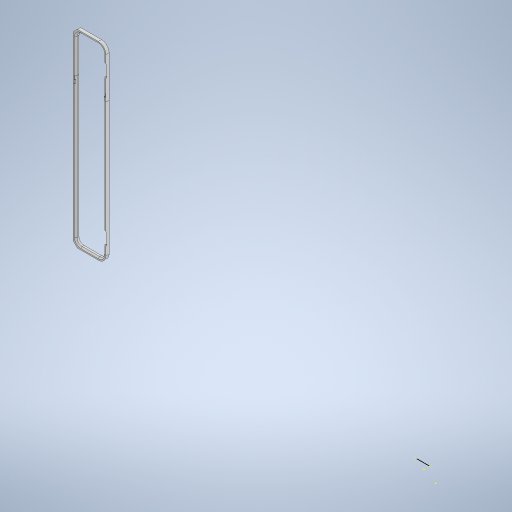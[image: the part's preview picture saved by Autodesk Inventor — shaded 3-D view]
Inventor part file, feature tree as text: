
AUTODESK INVENTOR PART (.ipt)
format: ipt  version: 2024.1 (Build 281209000, 209)  size: 7,057,408 bytes
history: native  units: mm
features: projected_geometry x112, sketch x92, extrude x87, chamfer x77, other x33, plane x15, fillet x9, pattern_linear x7, mirror x3, loft x2, pattern_circular x1, sweep x1
ambient origin geometry x8: Origin, YZ Plane, XZ Plane, XY Plane, X Axis, Y Axis, Z Axis, Center Point
bodies: Solid3 (feature_tree), Solid4 (feature_tree), Solid8 (feature_tree), Solid9 (feature_tree), Solid14 (feature_tree), Solid16 (feature_tree), Solid26 (feature_tree), Solid27 (feature_tree)
feature tree (439):
  other  "synth-a"
  other  "Blocks"
  extrude  "Extrusion1"  Depth=30.22mm
  plane  "Work Plane1"
  extrude  "Extrusion2"  Depth=17.13mm
  plane  "Work Plane2"
  mirror  "Mirror1"
  sketch  "Sketch3"  dims[d5=2.61mm d6=226.0mm]
  extrude  "Extrusion3"  Depth=226.0mm
  extrude  "Extrusion4"  Depth=8.2mm
  extrude  "Extrusion5"  Depth=35.4mm
  fillet  "Fillet1"  Radius=7.89mm
  pattern_linear  "Rectangular Pattern1"  Count1=56 Spacing1=0.0mm
  extrude  "Extrusion6"  Depth=3.14mm
  chamfer  "Chamfer1"  Distance=13.85mm
  chamfer  "Chamfer2"  Distance=440.5mm
  chamfer  "Chamfer3"  Distance=11.2mm
  chamfer  "Chamfer4"  Distance=3.1mm
  chamfer  "Chamfer5"  Distance=20.0mm
  chamfer  "Chamfer6"  Distance=7.26mm
  chamfer  "Chamfer7"  Distance=7.0mm Angle=45.0deg
  chamfer  "Chamfer8"  Distance=7.0mm Angle=45.0deg
  chamfer  "Chamfer9"  Distance=7.0mm Angle=45.0deg
  chamfer  "Chamfer10"  Distance=7.0mm Angle=45.0deg
  chamfer  "Chamfer11"  Distance=7.0mm Angle=45.0deg
  chamfer  "Chamfer12"  Distance=7.0mm Angle=45.0deg
  chamfer  "Chamfer13"  Distance=7.0mm Angle=45.0deg
  chamfer  "Chamfer14"  Distance=7.0mm Angle=45.0deg
  chamfer  "Chamfer15"  Distance=7.0mm Angle=45.0deg
  fillet  "Fillet2"  Radius=1.5mm
  pattern_linear  "Rectangular Pattern2"  Count1=3  [1 undecoded]
  extrude  "Extrusion7"  Depth=40.0mm
  extrude  "Extrusion8"  Depth=40.0mm
  plane  "Work Plane3"
  extrude  "Extrusion9"  Depth=20.42mm TaperAngle=0.0deg
  plane  "Work Plane7"
  plane  "Work Plane9"
  extrude  "Extrusion18"  Depth=60.6mm
  sketch  "Sketch26"  dims[d46=3.63mm]
  extrude  "Extrusion24"  Depth=35.8mm
  extrude  "Extrusion25"  Depth=2.9mm TaperAngle=0.0deg
  fillet  "Fillet3"  [1 undecoded]
  extrude  "Extrusion10"  Depth=20.0mm
  sketch  "Sketch12"  dims[d25=18.04mm]
  plane  "Work Plane5"
  extrude  "Extrusion12"  Depth=20.0mm
  extrude  "Extrusion14"  Depth=20.0mm
  extrude  "Extrusion15"  Depth=5.0mm
  plane  "Work Plane6"
  extrude  "Extrusion16"  Depth=16.580628mm
  mirror  "Mirror2"
  extrude  "Extrusion77"  Depth=20.0mm
  extrude  "Extrusion78"  Depth=5.0mm
  extrude  "Extrusion79"  Depth=2.0mm
  extrude  "Extrusion80"  Depth=2.5mm
  extrude  "Extrusion81"  Depth=2.5mm
  extrude  "Extrusion82"  Depth=2.5mm
  pattern_linear  "Rectangular Pattern4"  Count1=3 Spacing1=241.0mm
  chamfer  "Chamfer64"  Distance=10.0mm
  chamfer  "Chamfer65"  Distance=0.01mm
  chamfer  "Chamfer66"  Distance=10.0mm
  pattern_linear  "Rectangular Pattern3"  Count1=2 Spacing1=105.0mm
  pattern_linear  "Rectangular Pattern10"  Count1=2 Spacing1=0.0mm
  extrude  "Extrusion17"  Depth=2.0mm
  extrude  "Extrusion56"  Depth=4.0mm
  extrude  "Extrusion57"  Depth=3.0mm
  plane  "Work Plane8"
  plane  "Work Plane11"
  extrude  "Extrusion33"  Depth=4.0mm
  fillet  "Fillet6"  Radius=1.0mm
  extrude  "Extrusion29"  Depth=2.0mm
  extrude  "Extrusion31"  Depth=10.0mm
  extrude  "Extrusion32"  Depth=292.1mm
  extrude  "Extrusion34"  Depth=8.0mm
  extrude  "Extrusion35"  Depth=0.5mm TaperAngle=0.0deg
  extrude  "Extrusion36"  Depth=28.3mm
  fillet  "Fillet7"  Radius=28.3mm
  pattern_circular  "Circular Pattern1"  Count=7  [1 undecoded]
  extrude  "Extrusion37"  Depth=11.3mm
  plane  "Work Plane17"
  extrude  "Extrusion38"  Depth=13.54mm
  extrude  "Extrusion39"  Depth=22.0mm
  extrude  "Extrusion40"  Depth=2.0mm
  extrude  "Extrusion41"  Depth=2.0mm
  extrude  "Extrusion43"  Depth=2.0mm
  extrude  "Extrusion44"  Depth=2.0mm TaperAngle=0.0deg
  sketch  "Sketch47"  dims[d121=20.0mm d122=0.0mm d123=5.0mm]
  chamfer  "Chamfer18"  Distance=2.0mm Angle=45.0deg
  chamfer  "Chamfer19"  Distance=2.0mm
  chamfer  "Chamfer20"  Distance=13.0mm
  extrude  "Extrusion45"  Depth=2.0mm
  chamfer  "Chamfer21"  Distance=26.0mm
  extrude  "Extrusion46"  Depth=2.0mm TaperAngle=0.0deg
  extrude  "Extrusion49"  Depth=11.0mm
  extrude  "Extrusion50"  Depth=2.0mm TaperAngle=0.0deg
  plane  "Work Plane13"
  extrude  "Extrusion51"  Depth=10.0mm TaperAngle=0.0deg
  pattern_linear  "Rectangular Pattern7"  Spacing1=4.0mm  [1 undecoded]
  extrude  "Extrusion52"  Depth=2.0mm TaperAngle=0.0deg
  extrude  "Extrusion53"  Depth=2.0mm
  extrude  "Extrusion54"  Depth=2.0mm TaperAngle=0.0deg
  extrude  "Extrusion55"  Depth=2.0mm TaperAngle=45.0deg
  chamfer  "Chamfer22"  Distance=2.0mm
  chamfer  "Chamfer23"  Distance=150.0mm
  chamfer  "Chamfer24"  Distance=0.02mm
  chamfer  "Chamfer25"  Distance=15.0mm
  extrude  "Extrusion74"  Depth=2.0mm TaperAngle=0.0deg
  chamfer  "Chamfer58"  Distance=7.0mm
  chamfer  "Chamfer59"  Distance=5.0mm
  plane  "Work Plane16"
  extrude  "Extrusion73"  Depth=2.0mm
  plane  "Work Plane14"
  extrude  "Extrusion75"  Depth=2.0mm
  chamfer  "Chamfer60"  Distance=2.5mm
  plane  "Work Plane15"
  extrude  "Extrusion71"  Depth=2.0mm TaperAngle=0.0deg
  extrude  "Extrusion72"  Depth=2.0mm
  chamfer  "Chamfer61"  Distance=7.0mm
  chamfer  "Chamfer62"  Distance=10.5mm
  extrude  "Extrusion83"  Depth=241.0mm
  extrude  "Extrusion84"  Depth=2.0mm
  extrude  "Extrusion85"  Depth=2.0mm
  extrude  "Extrusion86"  TaperAngle=90.0deg  [1 undecoded]
  extrude  "Extrusion87"  Depth=2.0mm
  loft  "Loft2"
  chamfer  "Chamfer68"  Distance=420.0mm
  chamfer  "Chamfer69"  Distance=7.0mm
  chamfer  "Chamfer70"  Distance=40.0mm
  chamfer  "Chamfer71"  Distance=7.0mm
  chamfer  "Chamfer72"  Distance=10.0mm
  chamfer  "Chamfer73"  Distance=4.2mm
  chamfer  "Chamfer79"  [1 undecoded]
  chamfer  "Chamfer80"  Distance=2.5mm
  chamfer  "Chamfer81"  Distance=8.0mm
  chamfer  "Chamfer82"  Distance=10.0mm
  chamfer  "Chamfer83"  Distance=1.5mm
  sketch  "Sketch109"  dims[d216=16.2mm d217=28.3mm d218=28.3mm]
  extrude  "Extrusion91"  Depth=1.0mm
  chamfer  "Chamfer84"  Distance=1.0mm
  chamfer  "Chamfer85"  Distance=160.0mm Angle=360.0deg
  chamfer  "Chamfer86"  Distance=13.0mm
  chamfer  "Chamfer87"  Distance=1.5mm
  pattern_linear  "Rectangular Pattern9"  Spacing1=1.2mm  [1 undecoded]
  extrude  "Extrusion58"  Depth=2.0mm TaperAngle=0.0deg
  extrude  "Extrusion59"  Depth=2.0mm TaperAngle=0.0deg
  chamfer  "Chamfer26"  Distance=7.1mm
  chamfer  "Chamfer27"  Distance=2.0mm
  chamfer  "Chamfer28"  Distance=8.8mm
  chamfer  "Chamfer29"  Distance=48.0mm
  chamfer  "Chamfer30"  Distance=30.0mm
  chamfer  "Chamfer31"  Distance=40.0mm
  chamfer  "Chamfer32"  Distance=43.0mm
  extrude  "Extrusion60"  Depth=2.0mm
  extrude  "Extrusion61"  Depth=2.0mm
  loft  "Loft1"
  extrude  "Extrusion62"  Depth=2.0mm
  sweep  "Sweep1"
  chamfer  "Chamfer33"  Distance=11.5mm
  chamfer  "Chamfer35"  Distance=8.0mm
  chamfer  "Chamfer36"  Distance=4.0mm
  extrude  "audio-io-device"  Depth=2.0mm
  fillet  "Fillet4"  Radius=3.0mm
  extrude  "Extrusion20"  Depth=10.0mm TaperAngle=0.0deg
  extrude  "Extrusion21"  Depth=10.0mm TaperAngle=0.0deg
  extrude  "Extrusion22"  Depth=8.0mm TaperAngle=45.0deg
  chamfer  "Chamfer16"  Distance=2.0mm Angle=45.0deg
  fillet  "Fillet5"  Radius=4.0mm
  extrude  "Extrusion23"  Depth=2.0mm
  extrude  "Extrusion92"  Depth=23.0mm
  fillet  "Fillet8"  Radius=10.0mm
  extrude  "Extrusion26"  Depth=20.0mm
  extrude  "Extrusion27"  Depth=8.0mm TaperAngle=45.0deg
  chamfer  "Chamfer17"  Distance=2.5mm
  plane  "Work Plane10"
  mirror  "Mirror3"
  extrude  "Extrusion28"  Depth=10.0mm
  extrude  "io-device-clip"  Depth=10.0mm TaperAngle=0.0deg
  extrude  "Extrusion93"  Depth=20.0mm
  fillet  "Fillet9"  Radius=1.5mm
  extrude  "Extrusion64"  Depth=2.0mm
  extrude  "Extrusion65"  Depth=1.0mm
  extrude  "Extrusion66"  Depth=1.0mm
  extrude  "Extrusion67"  Depth=5.75mm
  chamfer  "Chamfer38"  Distance=3.0mm
  extrude  "Extrusion69"  Depth=2.0mm
  extrude  "Extrusion70"  Depth=2.0mm
  chamfer  "Chamfer48"  Angle=90.0deg  [1 undecoded]
  chamfer  "Chamfer49"  Distance=1.5mm
  chamfer  "Chamfer50"  Distance=1.5mm
  chamfer  "Chamfer51"  Distance=1.5mm
  chamfer  "Chamfer52"  Distance=1.5mm
  chamfer  "Chamfer53"  Distance=1.5mm
  chamfer  "Chamfer54"  Distance=1.5mm
  chamfer  "Chamfer55"  Distance=9.0mm
  chamfer  "Chamfer56"  Distance=4.0mm
  chamfer  "Chamfer57"  Distance=9.0mm
  chamfer  "Chamfer74"  Distance=10.0mm
  chamfer  "Chamfer75"  Distance=20.0mm
  chamfer  "Chamfer76"  Distance=0.02mm
  chamfer  "Chamfer77"  Distance=0.02mm
  chamfer  "Chamfer78"  Distance=9.0mm
  extrude  "Extrusion88"  Depth=15.0mm TaperAngle=0.0deg
  extrude  "Extrusion89"  Depth=22.0mm
  extrude  "Extrusion94"  Depth=2.0mm
  extrude  "Extrusion95"  Depth=2.0mm TaperAngle=0.0deg
  chamfer  "Chamfer88"  Distance=4.5mm
  chamfer  "Chamfer89"  Distance=48.0mm
  chamfer  "Chamfer90"  Distance=9.0mm
  extrude  "Extrusion96"  Depth=2.0mm
  sketch  "Sketch1"  dims[d0=205.0mm d1=30.22mm]
  sketch  "Sketch2"  dims[d2=102.5mm d3=17.13mm]
  projected_geometry  "Projected Loop1"
  sketch  "Sketch4"  dims[d7=12.4mm d8=8.2mm]
  projected_geometry  "Projected Loop2"
  sketch  "Sketch5"  dims[d9=4.5mm d10=35.4mm d11=7.89mm]
  sketch  "Sketch6"  dims[d12=9.657689mm]
  projected_geometry  "Projected Loop3"
  sketch  "Sketch7"  dims[d13=17.466067mm d14=560.0mm d15=0.0mm]
  sketch  "Sketch8"  dims[d16=-18.52mm d17=3.14mm d18=13.85mm d19=0.0mm]
  sketch  "Sketch9"  dims[d20=17.38mm]
  sketch  "Sketch10"  dims[d21=91.58mm d22=440.5mm d23=0.0mm]
  projected_geometry  "Projected Loop4"
  projected_geometry  "Projected Loop5"
  projected_geometry  "Projected Loop6"
  other  "stand-leg-A"
  other  "Pattern of stand-leg-A:1"
  other  "Pattern of stand-leg-A:2"
  sketch  "Sketch11"  dims[d24=2.4mm]
  sketch  "Sketch14"  dims[d26=18.56mm d27=11.2mm d28=0.0mm]
  projected_geometry  "Projected Loop8"
  sketch  "Sketch15"  dims[d29=81.62mm d30=3.1mm d31=0.0mm]
  sketch  "Sketch17"  dims[d32=1.5mm d33=220.0mm d35=20.0mm]
  projected_geometry  "Projected Loop10"
  projected_geometry  "Projected Loop11"
  projected_geometry  "Projected Loop12"
  projected_geometry  "Projected Loop13"
  sketch  "Sketch18"  dims[d36=48.6mm]
  sketch  "Sketch19"  dims[d37=8.7mm]
  projected_geometry  "Projected Loop14"
  projected_geometry  "Projected Loop15"
  projected_geometry  "Projected Loop16"
  projected_geometry  "Projected Loop17"
  projected_geometry  "Projected Loop18"
  projected_geometry  "Projected Loop19"
  projected_geometry  "Projected Loop20"
  projected_geometry  "Projected Loop21"
  other  "crossbars"
  sketch  "Sketch20"  dims[d38=8.7mm]
  sketch  "Sketch21"  dims[d39=8.7mm]
  other  "audio-io"
  sketch  "Sketch22"  dims[d40=8.7mm]
  projected_geometry  "Projected Loop22"
  sketch  "Sketch23"  dims[d41=8.7mm]
  sketch  "Sketch24"  dims[d44=3.63mm]
  sketch  "Sketch25"  dims[d45=3.63mm]
  projected_geometry  "Projected Loop23"
  sketch  "Sketch27"  dims[d47=3.63mm]
  projected_geometry  "Projected Loop24"
  other  "audio-io-stand"
  sketch  "Sketch28"  dims[d48=3.63mm]
  projected_geometry  "Projected Loop25"
  sketch  "Sketch29"  dims[d49=3.63mm d50=7.26mm d51=0.0mm d52=5.0mm d53=7.0mm d54=45.0deg d55=5.0mm d56=7.0mm d57=45.0deg d58=5.0mm d59=7.0mm d60=45.0deg d61=5.0mm d62=7.0mm d63=45.0deg d64=5.0mm d65=7.0mm d66=45.0deg d67=1.5mm d68=7.0mm d69=45.0deg d70=1.5mm d71=7.0mm d72=45.0deg d73=1.5mm d74=7.0mm d75=45.0deg d76=1.5mm d77=7.0mm d78=45.0deg]
  sketch  "Sketch30"  dims[d79=1.5mm d80=7.0mm d81=45.0deg]
  projected_geometry  "Projected Loop26"
  sketch  "Sketch34"  dims[d82=1.5mm d83=7.0mm d84=45.0deg]
  projected_geometry  "Projected Loop29"
  sketch  "Sketch35"  dims[d85=1.5mm d86=7.0mm d87=45.0deg]
  other  "back-uprights"
  projected_geometry  "Projected Loop30"
  sketch  "Sketch36"  dims[d88=1.5mm d89=7.0mm d90=45.0deg]
  other  "looper"
  sketch  "Sketch37"  dims[d91=1.5mm d92=7.0mm d93=45.0deg]
  sketch  "Sketch38"  dims[d94=1.5mm d95=7.0mm d96=45.0deg d97=1.5mm d98=30.0mm d100=140.0mm]
  sketch  "Sketch39"  dims[d101=17.93mm d102=40.0mm]
  sketch  "Sketch40"  dims[d103=40.0mm d104=40.0mm]
  sketch  "Sketch41"  dims[d105=35.4mm d106=20.42mm d107=0.0mm]
  projected_geometry  "Projected Loop31"
  projected_geometry  "Projected Loop32"
  other  "top-arm"
  sketch  "Sketch42"  dims[d108=20.16mm d109=60.6mm]
  projected_geometry  "Projected Loop33"
  sketch  "Sketch43"  dims[d110=60.6mm d111=35.8mm]
  projected_geometry  "Projected Loop34"
  sketch  "Sketch44"  dims[d112=52.9mm d113=2.9mm d114=0.0mm d115=-10.0mm]
  sketch  "Sketch45"  dims[d116=20.0mm d118=90.0mm]
  projected_geometry  "Projected Loop35"
  sketch  "Sketch46"  dims[d119=10.0mm d120=20.0mm]
  projected_geometry  "Projected Loop36"
  projected_geometry  "Projected Loop37"
  sketch  "Sketch48"  dims[d124=5.0mm d125=5.0mm]
  projected_geometry  "Projected Loop38"
  sketch  "Sketch50"  dims[d126=30.0mm d127=16.580628mm]
  projected_geometry  "Projected Loop40"
  other  "Pattern of back-uprights:3"
  other  "Pattern of back-uprights:4"
  sketch  "Sketch57"  dims[d128=8.0mm d129=20.0mm]
  projected_geometry  "Projected Loop42"
  projected_geometry  "Projected Loop43"
  sketch  "Sketch58"  dims[d133=5.0mm d134=5.0mm]
  projected_geometry  "Projected Loop44"
  sketch  "Sketch59"  dims[d135=18.0mm d136=2.0mm]
  projected_geometry  "Projected Loop45"
  projected_geometry  "Projected Loop46"
  projected_geometry  "Projected Loop47"
  sketch  "Sketch60"  dims[d139=120.0mm d140=2.5mm]
  projected_geometry  "Projected Loop48"
  projected_geometry  "Projected Loop49"
  other  "back-crossbeam"
  sketch  "Sketch61"  dims[d141=2.5mm d142=2.5mm]
  projected_geometry  "Projected Loop50"
  sketch  "Sketch62"  dims[d143=2.5mm d144=2.5mm]
  other  "sqr-connector"
  other  "sqr-connector_1"
  other  "sqr-connector_2"
  sketch  "Sketch63"  dims[d145=2.5mm]
  projected_geometry  "Projected Loop51"
  projected_geometry  "Projected Loop52"
  projected_geometry  "Projected Loop53"
  sketch  "Sketch66"  dims[d146=95.0mm]
  projected_geometry  "Projected Loop55"
  sketch  "Sketch67"  dims[d147=2.5mm d148=30.0mm d150=241.0mm]
  projected_geometry  "Projected Loop56"
  projected_geometry  "Projected Loop57"
  projected_geometry  "Projected Loop58"
  projected_geometry  "Projected Loop59"
  projected_geometry  "Projected Loop60"
  projected_geometry  "Projected Loop61"
  projected_geometry  "Projected Loop62"
  projected_geometry  "Projected Loop63"
  projected_geometry  "Projected Loop64"
  projected_geometry  "Projected Loop65"
  sketch  "Sketch68"  dims[d151=2.0mm]
  projected_geometry  "Projected Loop66"
  projected_geometry  "Projected Loop67"
  sketch  "Sketch69"  dims[d152=10.0mm]
  projected_geometry  "Projected Loop68"
  projected_geometry  "Projected Loop69"
  other  "TOP-CROSSBEAM"
  sketch  "Sketch70"  dims[d153=7.0mm]
  projected_geometry  "Projected Loop70"
  other  "angled-member"
  sketch  "Sketch71"  dims[d154=10.0mm]
  projected_geometry  "Projected Loop71"
  other  "Edges1"
  other  "Edges2"
  sketch  "Sketch74"  dims[d155=6.5mm]
  projected_geometry  "Projected Loop74"
  sketch  "Sketch75"  dims[d156=6.5mm]
  projected_geometry  "Projected Loop75"
  sketch  "Sketch76"  dims[d158=0.01mm]
  sketch  "Sketch77"  dims[d159=5.0mm]
  projected_geometry  "Projected Loop76"
  sketch  "Sketch78"  dims[d161=8.0mm]
  projected_geometry  "Projected Loop77"
  sketch  "Sketch79"  dims[d162=0.01mm]
  projected_geometry  "Projected Loop78"
  sketch  "Sketch80"  dims[d163=15.0mm]
  projected_geometry  "Projected Loop79"
  projected_geometry  "Projected Loop80"
  projected_geometry  "Projected Loop81"
  sketch  "Sketch81"  dims[d164=2.0mm d165=10.0mm d166=0.0mm d169=0.01mm d170=0.0mm]
  projected_geometry  "Projected Loop82"
  sketch  "Sketch83"  dims[d171=0.01mm d174=10.0mm d175=0.0mm]
  sketch  "Sketch85"  dims[d176=0.01mm d177=0.0mm]
  projected_geometry  "Projected Loop83"
  projected_geometry  "Projected Loop84"
  projected_geometry  "Projected Loop85"
  sketch  "Sketch86"  dims[d178=8.0mm]
  sketch  "Sketch88"  dims[d179=7.0mm]
  sketch  "Sketch89"  dims[d180=-8.0mm]
  projected_geometry  "Projected Loop87"
  sketch  "Sketch90"  dims[d181=6.0mm]
  projected_geometry  "Projected Loop88"
  sketch  "Sketch91"  dims[d182=4.0mm]
  sketch  "Sketch94"  dims[d183=3.0mm]
  sketch  "Sketch95"  dims[d184=3.0mm]
  sketch  "Sketch96"  dims[d185=2.0mm]
  projected_geometry  "Projected Loop90"
  projected_geometry  "Projected Loop91"
  sketch  "Sketch97"  dims[d186=7.0mm d187=0.0mm d188=20.0mm d190=105.0mm d191=20.0mm d192=0.0mm]
  projected_geometry  "Projected Loop92"
  projected_geometry  "Projected Loop93"
  projected_geometry  "Projected Loop94"
  projected_geometry  "Projected Loop95"
  other  "feet"
  sketch  "Sketch98"  dims[d193=2.5mm d194=2.0mm]
  projected_geometry  "Projected Loop96"
  projected_geometry  "Projected Loop97"
  other  "rubber-top-base"
  sketch  "Sketch99"  dims[d195=90.0deg d196=4.0mm d197=7.0mm]
  projected_geometry  "Projected Loop98"
  other  "rubber-stopper"
  other  "Pattern of feet:7"
  other  "Pattern of feet:8"
  sketch  "Sketch100"  dims[d198=4.5mm d199=3.0mm]
  projected_geometry  "Projected Loop99"
  projected_geometry  "Projected Loop100"
  projected_geometry  "Projected Loop101"
  projected_geometry  "Projected Loop102"
  other  "rubber-toppers-top"
  sketch  "Sketch101"  dims[d200=4.0mm d201=4.0mm d202=1.0mm]
  projected_geometry  "Projected Loop103"
  other  "rubber-cap"
  sketch  "Sketch102"  dims[d203=7.0mm d204=2.0mm]
  projected_geometry  "Projected Loop104"
  other  "rubber-tip"
  sketch  "Sketch103"  dims[d205=13.0mm d206=0.0mm d207=10.0mm]
  projected_geometry  "Projected Loop105"
  sketch  "Sketch104"  dims[d208=107.0mm d209=292.1mm]
  projected_geometry  "Projected Loop106"
  other  "Edges3"
  other  "Edges4"
  sketch  "Sketch105"  dims[d210=43.8mm d211=0.0mm d212=8.0mm]
  projected_geometry  "Projected Loop107"
  sketch  "Sketch106"  dims[d213=1.59mm d214=0.5mm d215=0.0mm]
  projected_geometry  "Projected Loop108"
  projected_geometry  "Projected Loop110"
  sketch  "Sketch110"  dims[d219=28.3mm]
  projected_geometry  "Projected Loop111"
  sketch  "Sketch111"  dims[d220=23.9mm d221=70.0mm d222=0.0mm]
  projected_geometry  "Projected Loop112"
  projected_geometry  "Projected Loop113"
  sketch  "Sketch112"  dims[d223=11.7mm d224=11.3mm]
  projected_geometry  "Projected Loop114"
  projected_geometry  "Projected Loop115"
  projected_geometry  "Projected Loop116"
  projected_geometry  "Projected Loop117"
  projected_geometry  "Projected Loop118"
  sketch  "Sketch113"  dims[d225=13.54mm d226=13.54mm]
  projected_geometry  "Projected Loop119"
  sketch  "Sketch114"  dims[d227=22.0mm d228=60.0mm]
  projected_geometry  "Projected Loop120"
  projected_geometry  "Projected Loop121"
  projected_geometry  "Projected Loop122"
  projected_geometry  "Projected Loop123"
  projected_geometry  "Projected Loop124"
  sketch  "Sketch115"  dims[d229=30.0mm d230=30.0mm d231=30.0mm d232=13.0mm d233=15.4mm d234=0.0mm d235=5.0mm d236=2.0mm d237=45.0deg d238=2.0mm d239=13.0mm d240=13.0mm d241=26.0mm d242=42.0mm d243=0.0mm d244=11.0mm d245=42.0mm d246=0.0mm d247=10.0mm d248=0.0mm d255=4.0mm d256=100.0mm d257=0.0mm d258=5.0mm d259=2.0mm d260=0.0mm d261=2.0mm d262=2.0mm d263=45.0deg d269=2.0mm d270=0.0mm d271=150.0mm d272=0.02mm d273=15.0mm d274=0.0mm d279=14.55mm d280=0.0mm d282=7.0mm d283=5.0mm d285=5.0mm d287=2.5mm d288=2.5mm d289=14.55mm d290=0.0mm d292=17.0mm d293=7.0mm d294=10.5mm d295=30.0mm d297=241.0mm d298=100.0mm d300=32.16mm d301=90.0deg d302=54.4mm d303=90.0deg d304=420.0mm d305=0.0mm d306=7.0mm d307=40.0mm d308=7.0mm d309=10.0mm d310=0.0mm d311=4.2mm d312=0.0mm d313=0.0mm d314=2.5mm d315=8.0mm d316=10.0mm d317=1.5mm d318=0.0mm d319=1.0mm d320=1.0mm d321=160.0mm d322=360.0deg d324=13.0mm d325=1.5mm d326=0.0mm d327=1.2mm d328=0.0mm d329=2.5mm d330=0.0mm d331=3.5mm d332=0.0mm d333=7.1mm d334=2.0mm d335=0.0mm d337=8.8mm d338=48.0mm d339=30.0mm d340=40.0mm d341=43.0mm d342=135.0mm d343=36.0mm d344=22.0mm d345=146.0mm d346=12.0mm d347=11.5mm d348=8.0mm d349=4.0mm d350=2.0mm d351=3.0mm d354=10.0mm d355=0.0mm d356=10.0mm d357=0.0mm d360=8.0mm d361=2.0mm d362=45.0deg d363=5.0mm d364=2.0mm d365=45.0deg d366=4.0mm d367=2.0mm d368=45.0deg d370=36.0mm d371=23.0mm d372=10.0mm d373=0.0mm d374=20.0mm d376=8.0mm d377=2.0mm d378=45.0deg d379=2.5mm d380=10.0mm d381=10.0mm d382=0.0mm d422=20.0mm d423=1.5mm d424=1.5mm d425=1.0mm d426=1.0mm d427=5.75mm d428=3.0mm d430=6.5mm d431=6.5mm d432=90.0deg d433=1.5mm d434=1.5mm d435=1.5mm d436=1.5mm d437=1.5mm d438=1.5mm d439=9.0mm d440=0.0mm d441=4.0mm d442=9.0mm d443=0.0mm d444=10.0mm d445=0.0mm d446=20.0mm d447=0.02mm d448=0.02mm d449=9.0mm d450=0.0mm d451=15.0mm d452=0.0mm d453=20.0mm d454=1.5mm d455=1.5mm d456=1.0mm d457=1.0mm d458=5.75mm d459=3.0mm d460=6.5mm d461=6.5mm d462=90.0deg d463=1.5mm d464=1.5mm d465=1.5mm d466=1.5mm d467=1.5mm d468=1.5mm d485=20.0mm d486=1.5mm d487=1.5mm d488=1.0mm d489=1.0mm d490=5.75mm d491=3.0mm d492=6.5mm d493=6.5mm d494=90.0deg d495=1.5mm d496=1.5mm d497=1.5mm d498=1.5mm d499=1.5mm d500=1.5mm d501=20.0mm d502=1.5mm d503=1.5mm d504=1.0mm d505=1.0mm d506=5.75mm d507=3.0mm d508=6.5mm d509=6.5mm d510=90.0deg d511=1.5mm d512=1.5mm d513=1.5mm d514=1.5mm d515=1.5mm d516=1.5mm d517=22.0mm d518=120.0mm d519=9.0mm d520=0.0mm d521=4.5mm d522=48.0mm d523=9.0mm d524=0.0mm d525=2.5mm d526=2.5mm d527=2.0mm d528=2.0mm d529=6.0mm d530=4.5mm d531=30.0deg d532=3.3mm d533=10.0mm d534=2.0mm d535=45.0deg d536=7.0mm d537=2.0mm d538=45.0deg d539=3.0mm d540=2.0mm d541=45.0deg d542=3.0mm d543=2.0mm d544=45.0deg d545=0.02mm d546=0.02mm d547=10.0mm d548=0.0mm d549=8.0mm d550=8.0mm d552=20.0mm d553=20.0mm d554=8.0mm d555=8.0mm d556=20.0mm d558=20.0mm d559=0.0mm d560=0.0mm d561=10.0mm d562=0.0mm d563=5.0mm d564=0.0mm d565=2.0mm d566=2.0mm d567=45.0deg d568=1.0mm d569=2.0mm d570=45.0deg d571=2.0mm d572=2.0mm d573=45.0deg d574=1.0mm d575=2.0mm d576=45.0deg d577=4.0mm d578=2.0mm d579=45.0deg d580=2.0mm d581=2.0mm d582=45.0deg d583=4.0mm d584=2.0mm d585=45.0deg d586=0.02mm d587=8.0mm d588=15.0mm d589=0.0mm d590=0.02mm d591=8.0mm d592=9.8mm d593=0.0mm d594=0.0mm d595=90.0deg d596=0.0mm d597=90.0deg d598=9.8mm d599=0.0mm d600=0.0mm d601=0.0mm d602=2.0mm d603=2.0mm d604=45.0deg d608=2.0mm d609=2.0mm d610=45.0deg d611=3.0mm d612=2.0mm d613=45.0deg d614=0.02mm d615=9.0mm d616=0.0mm d617=9.0mm d618=0.0mm d619=0.02mm d620=7.0mm d621=0.0mm d622=49.5mm d623=0.0mm d624=1.0mm d625=0.0mm d634=6.5mm d635=2.0mm d636=45.0deg d643=30.0mm d644=30.0mm d645=0.0mm d667=0.0mm d668=60.0mm d669=19.35mm d670=7.75mm d671=0.0mm d672=0.0mm d673=8.0mm d674=2.0mm d675=45.0deg d676=8.0mm d677=2.0mm d678=45.0deg d679=2.0mm d680=2.0mm d681=45.0deg d682=2.0mm d683=2.0mm d684=45.0deg d685=2.0mm d686=2.0mm d687=45.0deg d688=2.0mm d689=2.0mm d690=45.0deg d691=2.0mm d692=2.0mm d693=45.0deg d694=2.0mm d695=2.0mm d696=45.0deg d697=8.0mm d698=2.0mm d699=45.0deg d700=8.0mm d701=2.0mm d702=45.0deg d713=2.0mm d714=0.0mm d719=4.0mm d720=4.0mm d721=2.0mm d722=0.0mm d728=2.0mm d729=0.0mm d730=0.0mm d731=0.0mm d732=4.0mm d733=2.0mm d734=45.0deg d735=3.0mm d736=2.0mm d737=45.0deg d738=27.925268mm d739=27.925268mm d743=2.0mm d744=0.0mm d747=1.0mm d748=1.0mm d749=1.89128mm d750=1.89128mm d751=1.5mm d754=1.79mm d755=2.0mm d756=45.0deg d757=4.0mm d758=2.0mm d759=4.0mm d760=4.0mm d761=4.0mm d762=4.0mm d763=4.0mm d764=4.0mm d765=3.0mm d766=3.0mm d767=3.0mm d768=2.0mm d769=20.0mm d771=241.0mm d772=2.0mm d773=2.0mm d774=45.0deg d775=2.0mm d776=2.0mm d777=45.0deg d781=7.0mm d782=4.0mm d783=3.0mm d784=3.0mm d785=18.0mm d786=16.0mm d787=2.0mm d788=0.0mm d789=1.5mm d790=1.5mm d791=2.0mm d792=0.0mm d793=6.0mm d795=3.0mm d796=20.0mm d798=20.0mm d799=2.0mm d800=20.0mm d801=2.0mm d802=0.0mm d803=20.0mm d804=0.3mm d805=0.3mm d806=0.3mm d807=0.3mm d808=2.0mm d809=2.0mm d810=2.0mm d811=2.0mm d812=2.0mm d813=2.0mm d814=2.0mm d815=2.0mm d816=2.0mm d817=2.0mm d818=2.0mm d819=2.0mm d820=2.0mm d821=2.0mm d822=2.0mm d823=2.0mm d824=2.0mm d825=2.0mm d826=2.0mm d827=2.0mm d828=2.0mm d829=2.0mm d830=2.0mm d831=2.0mm d832=2.0mm d833=2.0mm d834=2.0mm d835=2.0mm d836=2.0mm d837=2.0mm d838=2.0mm d839=2.0mm d840=4.0mm d841=0.0mm d842=0.3mm d843=0.3mm d844=2.0mm d845=2.0mm d846=2.0mm d847=2.0mm d848=2.0mm d849=2.0mm d850=2.0mm d851=2.0mm d852=2.0mm d853=2.0mm d854=2.0mm d855=2.0mm d856=2.0mm d857=2.0mm d858=2.0mm d859=2.0mm d860=3.0mm d861=0.0mm d862=0.3mm d863=2.0mm d864=2.0mm d865=2.0mm d866=2.0mm d867=2.0mm d868=2.0mm d869=2.0mm d870=2.0mm d871=3.0mm d872=0.0mm d873=30.0mm d875=241.0mm d876=0.3mm d877=0.3mm d878=0.3mm d879=0.3mm d880=2.0mm d881=2.0mm d882=2.0mm d883=2.0mm d884=2.0mm d885=2.0mm d886=2.0mm d887=2.0mm d888=2.0mm d889=2.0mm d890=2.0mm d891=2.0mm d892=2.0mm d893=2.0mm d894=2.0mm d895=2.0mm d896=2.0mm d897=2.0mm d898=2.0mm d899=2.0mm d900=2.0mm d901=2.0mm d902=2.0mm d903=2.0mm d904=2.0mm d905=2.0mm d906=2.0mm d907=2.0mm d908=2.0mm d909=2.0mm d910=2.0mm d911=2.0mm d912=3.0mm d913=0.0mm d914=1.0mm d915=2.0mm d916=45.0deg d917=1.0mm d918=2.0mm d919=45.0deg d920=1.0mm d921=2.0mm d922=45.0deg d923=0.3mm d924=2.0mm d925=2.0mm d926=2.0mm d927=2.0mm d928=2.0mm d929=2.0mm d930=2.0mm d931=2.0mm d932=3.0mm d933=0.0mm d934=0.3mm d935=3.0mm d936=0.0mm d937=0.3mm d938=3.0mm d939=0.0mm d940=0.25mm d941=0.0mm d942=0.0mm d943=90.0deg d944=0.0mm d945=90.0deg d949=1.0mm d950=2.0mm d951=45.0deg d952=1.0mm d953=2.0mm d954=45.0deg d955=1.0mm d956=2.0mm d957=45.0deg d958=1.0mm d959=2.0mm d960=45.0deg d961=1.0mm d962=2.0mm d963=45.0deg d964=1.0mm d965=2.0mm d966=45.0deg d967=1.0mm d968=2.0mm d969=45.0deg d970=1.5mm d971=2.0mm d972=45.0deg d973=1.5mm d974=2.0mm d975=45.0deg d976=1.5mm d977=2.0mm d978=45.0deg d979=5.0mm d980=2.0mm d981=45.0deg d982=0.25mm d983=0.0mm d984=10.0mm d985=0.0mm d1008=1.5mm d1009=7.0mm d1010=2.0mm d1011=45.0deg d1012=8.0mm d1013=2.0mm d1014=45.0deg d1015=5.0mm d1016=2.0mm d1017=45.0deg d1018=2.2mm d1019=2.0mm d1020=45.0deg d1021=4.0mm d1022=2.0mm d1023=45.0deg d1024=14.0mm d1025=6.0mm d1026=0.0mm d1027=0.0mm d1028=4.0mm d1029=2.0mm d1030=45.0deg d1031=3.0mm d1032=2.0mm d1033=45.0deg d1034=4.0mm d1035=2.0mm d1036=45.0deg d1037=4.0mm d1038=2.0mm d1039=45.0deg d1040=2.0mm d1041=2.0mm d1042=45.0deg d1043=2.0mm d1044=2.0mm d1045=45.0deg d1046=17.0mm d1047=31.0mm d1048=31.0mm d1049=22.0mm d1050=17.0mm d1051=2.0mm d1052=0.0mm d1053=1.0mm d1054=23.0mm d1055=12.0mm d1056=12.0mm d1057=12.0mm d1058=1.0mm d1059=1.0mm d1060=10.0mm d1061=0.0mm d1062=2.0mm d1063=10.0mm d1064=0.0mm d1065=4.0mm d1066=15.0mm d1067=2.7mm d1068=2.7mm d1069=1.5mm d1070=5.0mm d1071=5.0mm d1072=2.0mm d1073=10.0mm d1074=10.0mm d1075=0.05mm d1076=0.05mm d1077=25.9mm d1078=25.9mm d1079=0.5mm d1080=0.5mm d1081=0.5mm d1082=0.5mm d1083=0.5mm d1084=0.5mm d1085=0.5mm d1086=0.5mm d1087=0.5mm d1088=0.5mm d1089=0.2mm d1090=0.2mm d1091=0.2mm d1092=0.2mm d1093=0.0mm d1094=0.0mm d1095=2.0mm d1096=2.0mm d1097=45.0deg d1098=97.0mm d1099=0.0mm]
  other  "sqr-connector:1"
  other  "sqr-connector:2"
note: 8 required parameter values undecoded (feature->parameter linkage not recoverable at this tier; creation-order binding heuristic only, values carry confidence <= 0.55)
